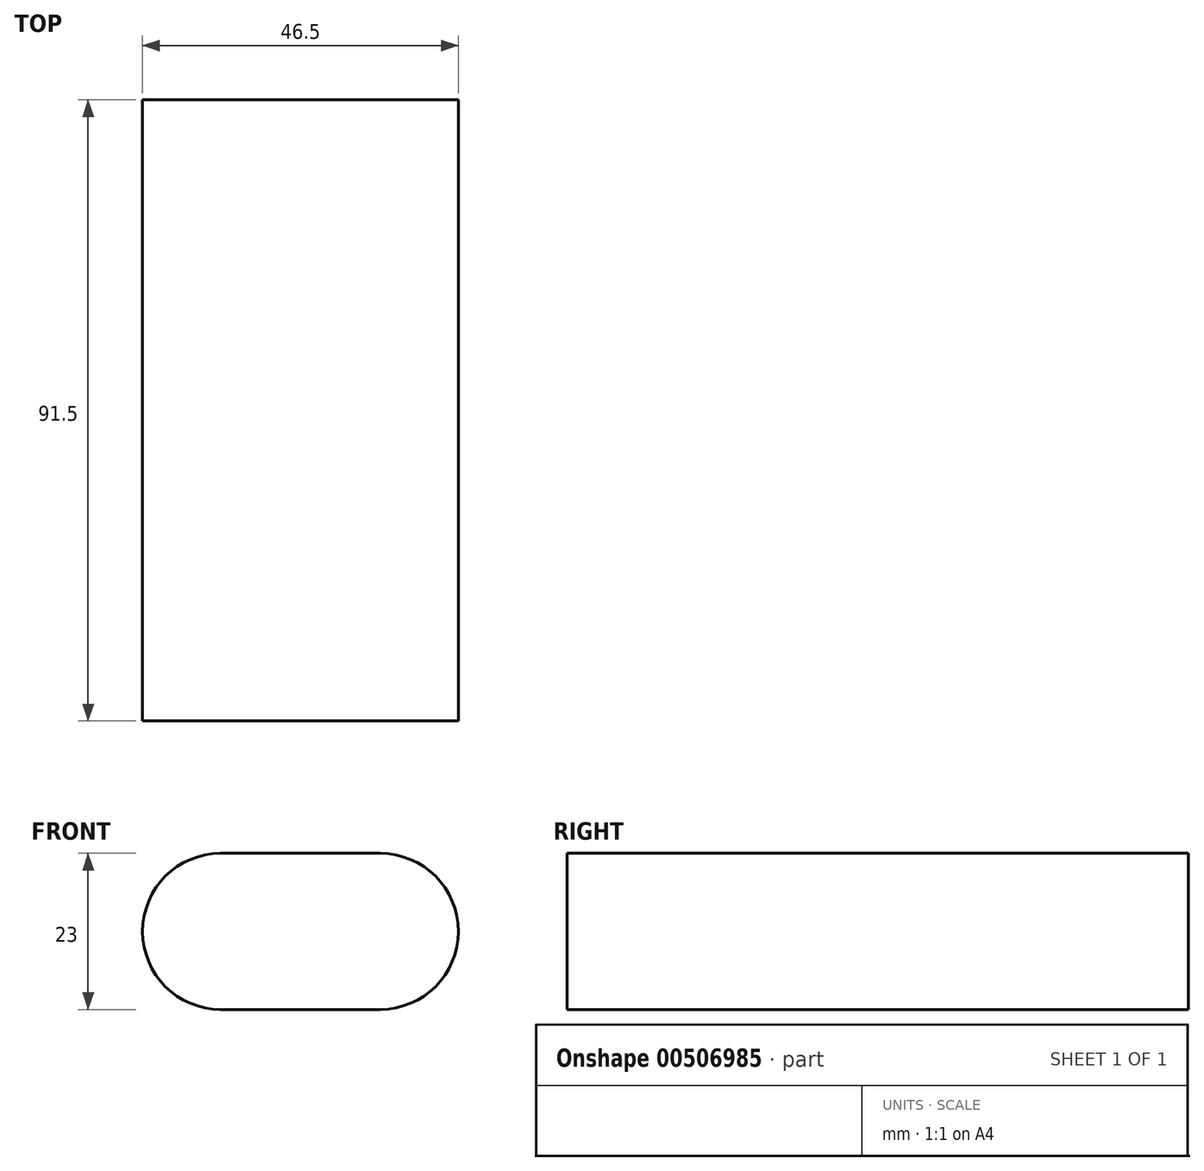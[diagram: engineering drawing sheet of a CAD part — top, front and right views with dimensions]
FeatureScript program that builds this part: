
annotation { "Feature Type Name" : "Feature", "Feature Type Description" : "" }
export const myFeature = defineFeature(function(context is Context, id is Id, definition is map)
    precondition{}
    {
        {
            var Q0;
            Q0=qCreatedBy(makeId("Front.planeOp"),FACE);
            var sketch = newSketch(context, id + "F0", { "sketchPlane" : qUnion([Q0])});
            skArc(sketch, "E0", {"start": v(-11.75, 11.5) * mm, "mid": v(-23.25, 0) * mm, "end": v(-11.75, -11.5) * mm});
            skArc(sketch, "E1", {"start": v(11.75, -11.5) * mm, "mid": v(23.25, 0) * mm, "end": v(11.75, 11.5) * mm});
            skLineSegment(sketch, "E2", {"start": v(-11.75, 0) * mm, "end": v(11.75, 0) * mm, "construction": true});
            skPoint(sketch, "E3", {"position": v(0, 0) * mm});
            skLineSegment(sketch, "E4", {"start": v(-11.75, 11.5) * mm, "end": v(11.75, 11.5) * mm});
            skLineSegment(sketch, "E5", {"start": v(-11.75, -11.5) * mm, "end": v(11.75, -11.5) * mm});
            skSolve(sketch);
        }
        {
            var Q0;
            Q0=makeQuery(id+"F0.imprint","IMPRINT",FACE,{"disambiguationData":[TD([[makeQuery(id+"F0.imprint","IMPRINT",EDGE,{"derivedFrom":sQuery(id+"F0.wireOp",EDGE,"E0")}),1.0]])]});
            extrude(context, id + "F1", {"entities" : qUnion([Q0]), "depth" : 91.5 * mm, "offsetDistance" : 25 * mm});
        }
    });
